# Revit family: 100_TLE25SL1A
name_source: partatom
category: 衛生器具
units: mm (PartAtom-declared; Revit-internal decimal feet)

## family parameters
OmniClass タイトル = Sanitary, Laundry, and Cleaning Equipment
OmniClass 番号 = 23.45.00.00
パーツ タイプ = 標準
ロード時にボイドで切り取り = はい
丸型コネクタ寸法 = 直径を使用
作業面ベース = いいえ
共有 = いいえ
常に垂直 = はい
部屋計算ポイント = いいえ

## types (1)
- TLE25SL1A
    3Dファイル形式 = rfa
    BLCJ仕様バージョン = Version1.0
    URL = https://jp.toto.com
    カウンター色 = <カテゴリ別>
    キーノート = 0表示の場合は商品仕様と設計数量をご確認ください
    データ作成ソフトVer = Revit ver.2019
    パネル色 = <カテゴリ別>
    モデル = TLE25SL1A
    上水負荷単位 = 0
    企業コード = 504860
    使用水 = 上水
    商品情報URL = https://www.com-et.com
    商品紹介URL = https://jp.toto.com
    奥行 = 201
    幅 = 48
    排気配管 = はい
    排水配管 = はい
    最低使用圧力 = 0.0 MPa
    最高使用圧力 = 0.0 MPa
    極数 = 2
    構成品番 = TLE25SL1A
    水配管 = はい
    温水配管 = はい
    相 = 1
    給湯負荷単位 = 0
    製品リリース年月 = 2022年08月
    製品出荷対象 = 国内
    製造元 = TOTO株式会社
    説明 = 台付自動水栓_コンテンポラリタイプ（角）_高さ252mm
    負荷分類 = 9_コンセント
    陶器色 = <カテゴリ別>
    電圧 = 100V
